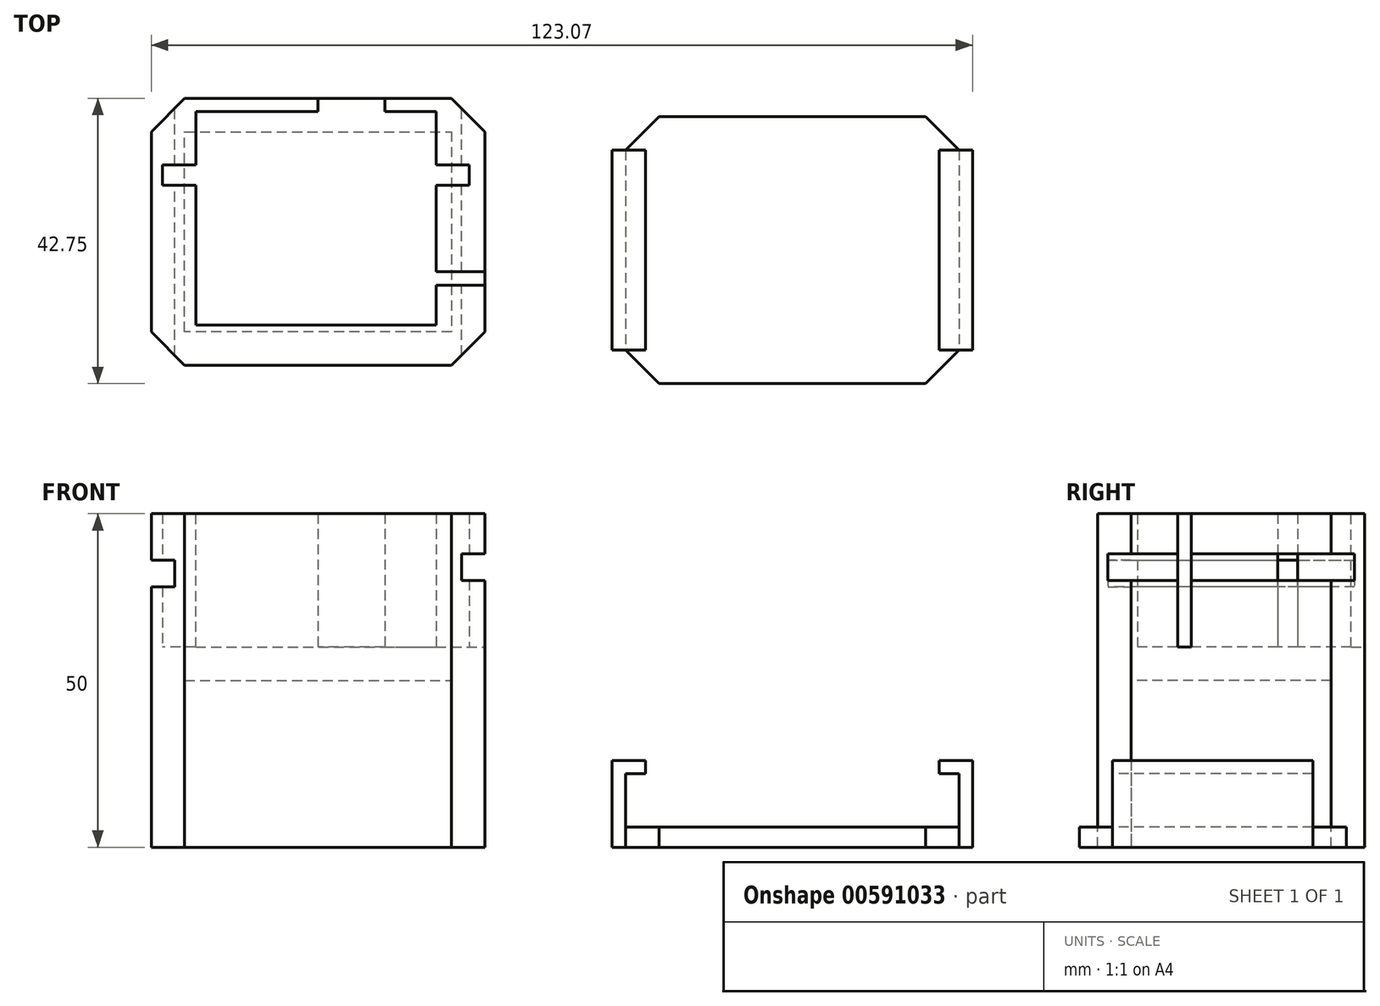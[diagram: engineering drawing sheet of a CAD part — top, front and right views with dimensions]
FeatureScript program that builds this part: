
annotation { "Feature Type Name" : "Feature", "Feature Type Description" : "" }
export const myFeature = defineFeature(function(context is Context, id is Id, definition is map)
    precondition{}
    {
        {
            var Q0;
            Q0=qCreatedBy(makeId("Top.planeOp"),FACE);
            var sketch = newSketch(context, id + "F0", { "sketchPlane" : qUnion([Q0])});
            skLineSegment(sketch, "E0.bottom", {"start": v(-55.35, -8.66) * mm, "end": v(-5.35, -8.66) * mm});
            skLineSegment(sketch, "E0.top", {"start": v(-55.35, -48.66) * mm, "end": v(-5.35, -48.66) * mm});
            skLineSegment(sketch, "E0.left", {"start": v(-55.35, -8.66) * mm, "end": v(-55.35, -48.66) * mm});
            skLineSegment(sketch, "E0.right", {"start": v(-5.35, -8.66) * mm, "end": v(-5.35, -48.66) * mm});
            skSolve(sketch);
        }
        {
            var Q0;
            Q0 = qSketchRegion(id + "F0", true);
            extrude(context, id + "F1", {"entities" : qUnion([Q0]), "depth" : 50 * mm, "offsetDistance" : 25 * mm});
        }
        {
            var Q0;
            Q0=makeQuery(id+"F1.opExtrude","CAP_FACE",FACE,{"disambiguationData":[OSD([sQuery(id+"F0.wireOp",EDGE,"E0.bottom"),sQuery(id+"F0.wireOp",EDGE,"E0.top"),sQuery(id+"F0.wireOp",EDGE,"E0.left"),sQuery(id+"F0.wireOp",EDGE,"E0.right")])],"isStart":false});
            var sketch = newSketch(context, id + "F2", { "sketchPlane" : qUnion([Q0])});
            skLineSegment(sketch, "E1", {"start": v(-40, -48.66) * mm, "end": v(-40, -42.66) * mm});
            skLineSegment(sketch, "E2", {"start": v(-55.35, -40.71) * mm, "end": v(-51.35, -40.71) * mm});
            skLineSegment(sketch, "E3", {"start": v(-51.67, -8.66) * mm, "end": v(-51.67, -9.66) * mm});
            skLineSegment(sketch, "E4", {"start": v(-51.67, -9.66) * mm, "end": v(-51.67, -10.66) * mm});
            skLineSegment(sketch, "E5", {"start": v(-5.35, -33.61) * mm, "end": v(-9.35, -33.61) * mm});
            skLineSegment(sketch, "E6.bottom", {"start": v(-51.67, -10.66) * mm, "end": v(-9.67, -10.66) * mm});
            skLineSegment(sketch, "E6.top", {"start": v(-51.67, -42.66) * mm, "end": v(-9.67, -42.66) * mm});
            skLineSegment(sketch, "E6.left", {"start": v(-51.67, -10.66) * mm, "end": v(-51.67, -42.66) * mm});
            skLineSegment(sketch, "E6.right", {"start": v(-9.67, -10.66) * mm, "end": v(-9.67, -42.66) * mm});
            skSolve(sketch);
        }
        {
            var Q0;
            {var subQ1=sQuery(id+"F2.wireOp",EDGE,"E6.bottom");Q0=makeQuery(id+"F2.imprint","IMPRINT",FACE,{"disambiguationData":[TD([[makeQuery(id+"F2.imprint","IMPRINT",EDGE,{"derivedFrom":subQ1}),-1.0]])]});}
            extrude(context, id + "F3", {"entities" : qUnion([Q0]), "operationType" : NewBodyOperationType.REMOVE, "oppositeDirection" : true, "depth" : 20 * mm, "offsetDistance" : 25 * mm});
        }
        {
            var Q0;
            Q0=makeQuery(id+"F3.boolean.opBoolean","COPY",FACE,{"derivedFrom":makeQuery(id+"F3.opExtrude","SWEPT_FACE",FACE,{"disambiguationData":[OSD([sQuery(id+"F2.wireOp",EDGE,"E6.right")])]})});
            var sketch = newSketch(context, id + "F4", { "sketchPlane" : qUnion([Q0])});
            skLineSegment(sketch, "E7", {"start": v(42.66, 40) * mm, "end": v(21.66, 40) * mm});
            skLineSegment(sketch, "E8", {"start": v(21.66, 40) * mm, "end": v(18.66, 40) * mm});
            skLineSegment(sketch, "E9", {"start": v(18.66, 40) * mm, "end": v(10.66, 40) * mm});
            skLineSegment(sketch, "E10.bottom", {"start": v(18.66, 50) * mm, "end": v(10.66, 50) * mm});
            skLineSegment(sketch, "E10.top", {"start": v(18.66, 30) * mm, "end": v(10.66, 30) * mm});
            skLineSegment(sketch, "E10.left", {"start": v(18.66, 50) * mm, "end": v(18.66, 30) * mm});
            skLineSegment(sketch, "E10.right", {"start": v(10.66, 50) * mm, "end": v(10.66, 30) * mm});
            skLineSegment(sketch, "E11.bottom", {"start": v(21.66, 40) * mm, "end": v(42.66, 40) * mm});
            skLineSegment(sketch, "E11.top", {"start": v(21.66, 30) * mm, "end": v(42.66, 30) * mm});
            skLineSegment(sketch, "E11.left", {"start": v(21.66, 40) * mm, "end": v(21.66, 30) * mm});
            skLineSegment(sketch, "E11.right", {"start": v(42.66, 40) * mm, "end": v(42.66, 30) * mm});
            skLineSegment(sketch, "E12.top", {"start": v(21.66, 50) * mm, "end": v(42.66, 50) * mm});
            skLineSegment(sketch, "E12.left", {"start": v(21.66, 40) * mm, "end": v(21.66, 50) * mm});
            skLineSegment(sketch, "E12.right", {"start": v(42.66, 40) * mm, "end": v(42.66, 50) * mm});
            skSolve(sketch);
        }
        {
            var Q0;
            Q0 = qSketchRegion(id + "F4", true);
            extrude(context, id + "F5", {"entities" : qUnion([Q0]), "operationType" : NewBodyOperationType.ADD, "depth" : 3 * mm, "offsetDistance" : 25 * mm});
        }
        {
            var Q0;
            Q0=makeQuery(id+"F3.boolean.opBoolean","COPY",FACE,{"derivedFrom":makeQuery(id+"F3.opExtrude","SWEPT_FACE",FACE,{"disambiguationData":[OSD([sQuery(id+"F2.wireOp",EDGE,"E6.left")])]})});
            var sketch = newSketch(context, id + "F6", { "sketchPlane" : qUnion([Q0])});
            skLineSegment(sketch, "E13", {"start": v(-42.66, 40) * mm, "end": v(-21.66, 40) * mm});
            skLineSegment(sketch, "E14", {"start": v(-21.66, 40) * mm, "end": v(-18.66, 40) * mm});
            skLineSegment(sketch, "E15", {"start": v(-18.66, 40) * mm, "end": v(-10.66, 40) * mm});
            skLineSegment(sketch, "E16.bottom", {"start": v(-21.66, 50) * mm, "end": v(-42.66, 50) * mm});
            skLineSegment(sketch, "E16.top", {"start": v(-21.66, 30) * mm, "end": v(-42.66, 30) * mm});
            skLineSegment(sketch, "E16.left", {"start": v(-21.66, 50) * mm, "end": v(-21.66, 30) * mm});
            skLineSegment(sketch, "E16.right", {"start": v(-42.66, 50) * mm, "end": v(-42.66, 30) * mm});
            skPoint(sketch, "E17.oppositeSnap0", {"position": v(-26.66, 30) * mm});
            skLineSegment(sketch, "E17.bottom", {"start": v(-10.66, 50) * mm, "end": v(-18.66, 50) * mm});
            skLineSegment(sketch, "E17.top", {"start": v(-10.66, 30) * mm, "end": v(-18.66, 30) * mm});
            skLineSegment(sketch, "E17.left", {"start": v(-10.66, 50) * mm, "end": v(-10.66, 30) * mm});
            skLineSegment(sketch, "E17.right", {"start": v(-18.66, 50) * mm, "end": v(-18.66, 30) * mm});
            skSolve(sketch);
        }
        {
            var Q0;
            Q0 = qSketchRegion(id + "F6", true);
            extrude(context, id + "F7", {"entities" : qUnion([Q0]), "operationType" : NewBodyOperationType.ADD, "depth" : 3 * mm, "offsetDistance" : 25 * mm});
        }
        {
            var Q0;
            Q0=makeQuery(id+"F3.boolean.opBoolean","COPY",FACE,{"derivedFrom":makeQuery(id+"F3.opExtrude","SWEPT_FACE",FACE,{"disambiguationData":[OSD([sQuery(id+"F2.wireOp",EDGE,"E6.right")])]})});
            extrude(context, id + "F8", {"entities" : qUnion([Q0]), "operationType" : NewBodyOperationType.REMOVE, "oppositeDirection" : true, "depth" : 2 * mm, "offsetDistance" : 25 * mm});
        }
        {
            var Q0;
            Q0=makeQuery(id+"F3.boolean.opBoolean","COPY",FACE,{"derivedFrom":makeQuery(id+"F3.opExtrude","SWEPT_FACE",FACE,{"disambiguationData":[OSD([sQuery(id+"F2.wireOp",EDGE,"E6.left")])]})});
            extrude(context, id + "F9", {"entities" : qUnion([Q0]), "operationType" : NewBodyOperationType.REMOVE, "oppositeDirection" : true, "depth" : 2 * mm, "offsetDistance" : 25 * mm});
        }
        {
            var Q0;
            Q0=makeQuery(id+"F1.opExtrude","SWEPT_FACE",FACE,{"disambiguationData":[OSD([sQuery(id+"F0.wireOp",EDGE,"E0.bottom")])]});
            var sketch = newSketch(context, id + "F10", { "sketchPlane" : qUnion([Q0])});
            skLineSegment(sketch, "E18", {"start": v(55.35, 41.09) * mm, "end": v(30.35, 41.09) * mm});
            skLineSegment(sketch, "E19", {"start": v(30.35, 41.09) * mm, "end": v(20.35, 41.09) * mm});
            skLineSegment(sketch, "E20.bottom", {"start": v(20.35, 50) * mm, "end": v(30.35, 50) * mm});
            skLineSegment(sketch, "E20.top", {"start": v(20.35, 30) * mm, "end": v(30.35, 30) * mm});
            skLineSegment(sketch, "E20.left", {"start": v(20.35, 50) * mm, "end": v(20.35, 30) * mm});
            skLineSegment(sketch, "E20.right", {"start": v(30.35, 50) * mm, "end": v(30.35, 30) * mm});
            skSolve(sketch);
        }
        {
            var Q0;
            Q0 = qSketchRegion(id + "F10", true);
            extrude(context, id + "F11", {"entities" : qUnion([Q0]), "operationType" : NewBodyOperationType.REMOVE, "oppositeDirection" : true, "depth" : 5 * mm, "offsetDistance" : 25 * mm});
        }
        {
            var Q0;
            Q0=makeQuery(id+"F1.opExtrude","SWEPT_FACE",FACE,{"disambiguationData":[OSD([sQuery(id+"F0.wireOp",EDGE,"E0.right")])]});
            var sketch = newSketch(context, id + "F12", { "sketchPlane" : qUnion([Q0])});
            skLineSegment(sketch, "E21", {"start": v(-48.66, 45.68) * mm, "end": v(-34.66, 45.68) * mm});
            skLineSegment(sketch, "E22", {"start": v(-34.66, 45.68) * mm, "end": v(-36.66, 45.68) * mm});
            skLineSegment(sketch, "E23.bottom", {"start": v(-36.66, 50) * mm, "end": v(-34.66, 50) * mm});
            skLineSegment(sketch, "E23.top", {"start": v(-36.66, 30) * mm, "end": v(-34.66, 30) * mm});
            skLineSegment(sketch, "E23.left", {"start": v(-36.66, 50) * mm, "end": v(-36.66, 30) * mm});
            skLineSegment(sketch, "E23.right", {"start": v(-34.66, 50) * mm, "end": v(-34.66, 30) * mm});
            skSolve(sketch);
        }
        {
            var Q0;
            Q0 = qSketchRegion(id + "F12", true);
            extrude(context, id + "F13", {"entities" : qUnion([Q0]), "operationType" : NewBodyOperationType.REMOVE, "oppositeDirection" : true, "depth" : 10 * mm, "offsetDistance" : 25 * mm});
        }
        {
            var Q0;
            Q0=makeQuery(id+"F1.opExtrude","CAP_FACE",FACE,{"disambiguationData":[OSD([sQuery(id+"F0.wireOp",EDGE,"E0.bottom"),sQuery(id+"F0.wireOp",EDGE,"E0.top"),sQuery(id+"F0.wireOp",EDGE,"E0.left"),sQuery(id+"F0.wireOp",EDGE,"E0.right")])],"isStart":true});
            var sketch = newSketch(context, id + "F14", { "sketchPlane" : qUnion([Q0])});
            skLineSegment(sketch, "E24", {"start": v(-5.35, 13.66) * mm, "end": v(-10.35, 13.66) * mm});
            skLineSegment(sketch, "E25", {"start": v(-10.35, 13.66) * mm, "end": v(-10.35, 43.66) * mm});
            skLineSegment(sketch, "E26", {"start": v(-10.35, 43.66) * mm, "end": v(-50.35, 43.66) * mm});
            skLineSegment(sketch, "E27", {"start": v(-50.35, 43.66) * mm, "end": v(-50.35, 13.66) * mm});
            skLineSegment(sketch, "E28", {"start": v(-50.35, 13.66) * mm, "end": v(-10.35, 13.66) * mm});
            skSolve(sketch);
        }
        {
            var Q0;
            Q0=makeQuery(id+"F14.imprint","IMPRINT",FACE,{"disambiguationData":[TD([[makeQuery(id+"F14.imprint","IMPRINT",EDGE,{"derivedFrom":sQuery(id+"F14.wireOp",EDGE,"E25")}),1.0]])]});
            extrude(context, id + "F15", {"entities" : qUnion([Q0]), "operationType" : NewBodyOperationType.REMOVE, "oppositeDirection" : true, "depth" : 25 * mm, "offsetDistance" : 25 * mm});
        }
        {
            var Q0;
            Q0=qCreatedBy(makeId("Top.planeOp"),FACE);
            var sketch = newSketch(context, id + "F16", { "sketchPlane" : qUnion([Q0])});
            skLineSegment(sketch, "E29.bottom", {"start": v(15.72, -11.4) * mm, "end": v(65.72, -11.4) * mm});
            skLineSegment(sketch, "E29.top", {"start": v(15.72, -51.4) * mm, "end": v(65.72, -51.4) * mm});
            skLineSegment(sketch, "E29.left", {"start": v(15.72, -11.4) * mm, "end": v(15.72, -51.4) * mm});
            skLineSegment(sketch, "E29.right", {"start": v(65.72, -11.4) * mm, "end": v(65.72, -51.4) * mm});
            skSolve(sketch);
        }
        {
            var Q0;
            Q0 = qSketchRegion(id + "F16", true);
            extrude(context, id + "F17", {"entities" : qUnion([Q0]), "depth" : 3 * mm, "offsetDistance" : 25 * mm});
        }
        {
            var Q0;
            Q0=makeQuery(id+"F17.opExtrude","SWEPT_EDGE",EDGE,{"disambiguationData":[OSD([sQuery(id+"F16.wireOp",EDGE,"E29.bottom"),sQuery(id+"F16.wireOp",EDGE,"E29.right")])]});
            var Q1;
            Q1=makeQuery(id+"F17.opExtrude","SWEPT_EDGE",EDGE,{"disambiguationData":[OSD([sQuery(id+"F16.wireOp",EDGE,"E29.top"),sQuery(id+"F16.wireOp",EDGE,"E29.right")])]});
            var Q2;
            Q2=makeQuery(id+"F17.opExtrude","SWEPT_EDGE",EDGE,{"disambiguationData":[OSD([sQuery(id+"F16.wireOp",EDGE,"E29.top"),sQuery(id+"F16.wireOp",EDGE,"E29.left")])]});
            var Q3;
            Q3=makeQuery(id+"F17.opExtrude","SWEPT_EDGE",EDGE,{"disambiguationData":[OSD([sQuery(id+"F16.wireOp",EDGE,"E29.bottom"),sQuery(id+"F16.wireOp",EDGE,"E29.left")])]});
            chamfer(context, id + "F18", {"entities" : qUnion([Q0, Q1, Q2, Q3]), "width" : 5 * mm, "tangentPropagation" : true});
        }
        {
            var Q0;
            Q0=makeQuery(id+"F17.opExtrude","SWEPT_FACE",FACE,{"disambiguationData":[OSD([sQuery(id+"F16.wireOp",EDGE,"E29.right")])]});
            var Q1;
            Q1=makeQuery(id+"F17.opExtrude","SWEPT_FACE",FACE,{"disambiguationData":[OSD([sQuery(id+"F16.wireOp",EDGE,"E29.left")])]});
            extrude(context, id + "F19", {"entities" : qUnion([Q0, Q1]), "operationType" : NewBodyOperationType.ADD, "depth" : 2 * mm, "offsetDistance" : 25 * mm});
        }
        {
            var Q0;
            Q0=makeQuery(id+"F17.opExtrude","SWEPT_FACE",FACE,{"disambiguationData":[OSD([sQuery(id+"F16.wireOp",EDGE,"E29.left")])]});
            extrude(context, id + "F20", {"entities" : qUnion([Q0]), "operationType" : NewBodyOperationType.ADD, "depth" : 2 * mm, "offsetDistance" : 25 * mm});
        }
        {
            var Q0;
            {var subQ0=sQuery(id+"F16.wireOp",EDGE,"E29.left");var subQ1=sQuery(id+"F16.wireOp",EDGE,"E29.right");Q0=makeQuery(id+"F20.boolean.opBoolean","MERGE",FACE,{"derivedFrom":[makeQuery(id+"F19.boolean.opBoolean","MERGE",FACE,{"derivedFrom":[makeQuery(id+"F17.opExtrude","CAP_FACE",FACE,{"disambiguationData":[OSD([sQuery(id+"F16.wireOp",EDGE,"E29.bottom"),sQuery(id+"F16.wireOp",EDGE,"E29.top"),subQ0,subQ1])],"isStart":false}),makeQuery(id+"F19.opExtrude","SWEPT_FACE",FACE,{"disambiguationData":[OSD([subQ1]),TDD([makeQuery(id+"F17.opExtrude","CAP_EDGE",EDGE,{"disambiguationData":[OSD([subQ1])],"isStart":false})])]})]}),makeQuery(id+"F20.opExtrude","SWEPT_FACE",FACE,{"disambiguationData":[OSD([subQ0]),TDD([makeQuery(id+"F17.opExtrude","CAP_EDGE",EDGE,{"disambiguationData":[OSD([subQ0])],"isStart":false})])]})]});}
            var sketch = newSketch(context, id + "F21", { "sketchPlane" : qUnion([Q0])});
            skLineSegment(sketch, "E30.bottom", {"start": v(13.72, -16.4) * mm, "end": v(15.72, -16.4) * mm});
            skLineSegment(sketch, "E30.top", {"start": v(13.72, -46.4) * mm, "end": v(15.72, -46.4) * mm});
            skLineSegment(sketch, "E30.left", {"start": v(13.72, -16.4) * mm, "end": v(13.72, -46.4) * mm});
            skLineSegment(sketch, "E30.right", {"start": v(15.72, -16.4) * mm, "end": v(15.72, -46.4) * mm});
            skLineSegment(sketch, "E31.bottom", {"start": v(65.72, -16.4) * mm, "end": v(67.72, -16.4) * mm});
            skLineSegment(sketch, "E31.top", {"start": v(65.72, -46.4) * mm, "end": v(67.72, -46.4) * mm});
            skLineSegment(sketch, "E31.left", {"start": v(65.72, -16.4) * mm, "end": v(65.72, -46.4) * mm});
            skLineSegment(sketch, "E31.right", {"start": v(67.72, -16.4) * mm, "end": v(67.72, -46.4) * mm});
            skSolve(sketch);
        }
        {
            var Q0;
            Q0=makeQuery(id+"F21.imprint","IMPRINT",FACE,{"disambiguationData":[TD([[makeQuery(id+"F21.imprint","IMPRINT",EDGE,{"derivedFrom":sQuery(id+"F21.wireOp",EDGE,"E31.bottom")}),1.0]])]});
            var Q1;
            Q1=makeQuery(id+"F21.imprint","IMPRINT",FACE,{"disambiguationData":[TD([[makeQuery(id+"F21.imprint","IMPRINT",EDGE,{"derivedFrom":sQuery(id+"F21.wireOp",EDGE,"E30.bottom")}),-1.0]])]});
            extrude(context, id + "F22", {"entities" : qUnion([Q0, Q1]), "operationType" : NewBodyOperationType.ADD, "depth" : 10 * mm, "offsetDistance" : 25 * mm});
        }
        {
            var Q0;
            Q0=makeQuery(id+"F22.opExtrude","SWEPT_FACE",FACE,{"disambiguationData":[OSD([sQuery(id+"F21.wireOp",EDGE,"E31.left")])]});
            var sketch = newSketch(context, id + "F23", { "sketchPlane" : qUnion([Q0])});
            skLineSegment(sketch, "E32.bottom", {"start": v(16.4, 13) * mm, "end": v(46.4, 13) * mm});
            skLineSegment(sketch, "E32.top", {"start": v(16.4, 11) * mm, "end": v(46.4, 11) * mm});
            skLineSegment(sketch, "E32.left", {"start": v(16.4, 13) * mm, "end": v(16.4, 11) * mm});
            skLineSegment(sketch, "E32.right", {"start": v(46.4, 13) * mm, "end": v(46.4, 11) * mm});
            skSolve(sketch);
        }
        {
            var Q0;
            Q0 = qSketchRegion(id + "F23", true);
            extrude(context, id + "F24", {"entities" : qUnion([Q0]), "operationType" : NewBodyOperationType.ADD, "depth" : 3 * mm, "offsetDistance" : 25 * mm});
        }
        {
            var Q0;
            Q0=makeQuery(id+"F22.opExtrude","SWEPT_FACE",FACE,{"disambiguationData":[OSD([sQuery(id+"F21.wireOp",EDGE,"E30.right")])]});
            var sketch = newSketch(context, id + "F25", { "sketchPlane" : qUnion([Q0])});
            skLineSegment(sketch, "E33.bottom", {"start": v(-46.4, 13) * mm, "end": v(-16.4, 13) * mm});
            skLineSegment(sketch, "E33.top", {"start": v(-46.4, 11) * mm, "end": v(-16.4, 11) * mm});
            skLineSegment(sketch, "E33.left", {"start": v(-46.4, 13) * mm, "end": v(-46.4, 11) * mm});
            skLineSegment(sketch, "E33.right", {"start": v(-16.4, 13) * mm, "end": v(-16.4, 11) * mm});
            skSolve(sketch);
        }
        {
            var Q0;
            Q0 = qSketchRegion(id + "F25", true);
            extrude(context, id + "F26", {"entities" : qUnion([Q0]), "operationType" : NewBodyOperationType.ADD, "depth" : 3 * mm, "offsetDistance" : 25 * mm});
        }
        {
            var Q0;
            Q0=makeQuery(id+"F1.opExtrude","SWEPT_FACE",FACE,{"disambiguationData":[OSD([sQuery(id+"F0.wireOp",EDGE,"E0.left")])]});
            var sketch = newSketch(context, id + "F27", { "sketchPlane" : qUnion([Q0])});
            skLineSegment(sketch, "E34", {"start": v(13.03, 50) * mm, "end": v(13.03, 39) * mm});
            skLineSegment(sketch, "E35", {"start": v(13.03, 39) * mm, "end": v(48.66, 39) * mm});
            skLineSegment(sketch, "E36", {"start": v(48.66, 39) * mm, "end": v(48.66, 43) * mm});
            skLineSegment(sketch, "E37.bottom", {"start": v(48.66, 39) * mm, "end": v(8.66, 39) * mm});
            skLineSegment(sketch, "E37.top", {"start": v(48.66, 43) * mm, "end": v(8.66, 43) * mm});
            skLineSegment(sketch, "E37.right", {"start": v(8.66, 39) * mm, "end": v(8.66, 43) * mm});
            skSolve(sketch);
        }
        {
            var Q0;
            Q0 = qSketchRegion(id + "F27", true);
            extrude(context, id + "F28", {"entities" : qUnion([Q0]), "operationType" : NewBodyOperationType.REMOVE, "oppositeDirection" : true, "depth" : 3.5 * mm, "offsetDistance" : 25 * mm});
        }
        {
            var Q0;
            Q0=makeQuery(id+"F1.opExtrude","SWEPT_FACE",FACE,{"disambiguationData":[OSD([sQuery(id+"F0.wireOp",EDGE,"E0.right")])]});
            var sketch = newSketch(context, id + "F29", { "sketchPlane" : qUnion([Q0])});
            skLineSegment(sketch, "E38", {"start": v(-13.32, 50) * mm, "end": v(-13.32, 40) * mm});
            skLineSegment(sketch, "E39", {"start": v(-13.32, 40) * mm, "end": v(-48.66, 40) * mm});
            skLineSegment(sketch, "E40", {"start": v(-48.66, 40) * mm, "end": v(-48.66, 44) * mm});
            skLineSegment(sketch, "E41.bottom", {"start": v(-48.66, 44) * mm, "end": v(-8.66, 44) * mm});
            skLineSegment(sketch, "E41.top", {"start": v(-48.66, 40) * mm, "end": v(-8.66, 40) * mm});
            skLineSegment(sketch, "E41.left", {"start": v(-48.66, 44) * mm, "end": v(-48.66, 40) * mm});
            skLineSegment(sketch, "E41.right", {"start": v(-8.66, 44) * mm, "end": v(-8.66, 40) * mm});
            skSolve(sketch);
        }
        {
            var Q0;
            Q0 = qSketchRegion(id + "F29", true);
            extrude(context, id + "F30", {"entities" : qUnion([Q0]), "operationType" : NewBodyOperationType.REMOVE, "oppositeDirection" : true, "depth" : 3.5 * mm, "offsetDistance" : 25 * mm});
        }
        {
            var Q0;
            {var subQ0=sQuery(id+"F0.wireOp",EDGE,"E0.bottom");var subQ1=sQuery(id+"F0.wireOp",EDGE,"E0.right");Q0=makeQuery(id+"F30.boolean.opBoolean","SPLIT",EDGE,{"disambiguationData":[TD([makeQuery(id+"F30.opExtrude","SWEPT_FACE",FACE,{"disambiguationData":[OSD([sQuery(id+"F29.wireOp",EDGE,"E41.top")])]})])],"derivedFrom":makeQuery(id+"F1.opExtrude","SWEPT_EDGE",EDGE,{"disambiguationData":[OSD([subQ0,subQ1])]})});}
            var Q1;
            {var subQ0=sQuery(id+"F0.wireOp",EDGE,"E0.right");var subQ1=sQuery(id+"F0.wireOp",EDGE,"E0.top");Q1=makeQuery(id+"F30.boolean.opBoolean","SPLIT",EDGE,{"disambiguationData":[TD([makeQuery(id+"F30.opExtrude","SWEPT_FACE",FACE,{"disambiguationData":[OSD([sQuery(id+"F29.wireOp",EDGE,"E41.top")])]})])],"derivedFrom":makeQuery(id+"F1.opExtrude","SWEPT_EDGE",EDGE,{"disambiguationData":[OSD([subQ1,subQ0])]})});}
            var Q2;
            {var subQ0=sQuery(id+"F0.wireOp",EDGE,"E0.bottom");var subQ1=sQuery(id+"F0.wireOp",EDGE,"E0.left");Q2=makeQuery(id+"F28.boolean.opBoolean","SPLIT",EDGE,{"disambiguationData":[TD([makeQuery(id+"F28.opExtrude","SWEPT_FACE",FACE,{"disambiguationData":[OSD([sQuery(id+"F27.wireOp",EDGE,"E37.bottom")])]})])],"derivedFrom":makeQuery(id+"F1.opExtrude","SWEPT_EDGE",EDGE,{"disambiguationData":[OSD([subQ0,subQ1])]})});}
            var Q3;
            {var subQ0=sQuery(id+"F0.wireOp",EDGE,"E0.left");var subQ1=sQuery(id+"F0.wireOp",EDGE,"E0.top");Q3=makeQuery(id+"F28.boolean.opBoolean","SPLIT",EDGE,{"disambiguationData":[TD([makeQuery(id+"F28.opExtrude","SWEPT_FACE",FACE,{"disambiguationData":[OSD([sQuery(id+"F27.wireOp",EDGE,"E37.bottom")])]})])],"derivedFrom":makeQuery(id+"F1.opExtrude","SWEPT_EDGE",EDGE,{"disambiguationData":[OSD([subQ1,subQ0])]})});}
            chamfer(context, id + "F31", {"entities" : qUnion([Q0, Q1, Q2, Q3]), "width" : 5 * mm, "tangentPropagation" : true});
        }
    });
